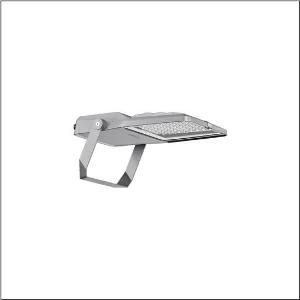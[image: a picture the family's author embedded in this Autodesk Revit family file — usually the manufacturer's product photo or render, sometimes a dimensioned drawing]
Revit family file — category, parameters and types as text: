
# Revit family: floodlight_fl_21_iq_mini___pl61_5xa7772c3c1a_b73e
name_source: partatom
category: Lighting Fixtures
units: mm (PartAtom-declared; Revit-internal decimal feet)

## family parameters
Cut with Voids When Loaded = No
Host = Face
Light Source = No
Part Type = Normal
Room Calculation Point = No
Round Connector Dimension = Use Diameter
Shared = No

## types (1)
- --- (1 x LED, 10320 lm, 87.2 W, 3000K)
    Apparent Load = 87 VA
    CIE Flux Codes = 33 65 98 100 100
    Color Rendering = 80
    Color Temperature = 3000K
    Default Elevation = 1800 mm
    Description = Floodlight FL 21 iQ mini, floodlight, primary light control with lens, of PMMA, primary optical cover: protective disc, of toughened safety glass, transparent, light distribution: PL61, light emission: direct distribution, installation type: surface-mounted, LED, High Power LED, rated luminous flux: 10.320lm, luminous efficacy: 118lm/W, light colour: 830, colour temperature: 3000K, control: Street-Remote, Auto-Match, Temp-Guard, Night-Set, Smart-Wire, Desk-Remote (wireless, voltage-free reading and setting of iQ features in the workshop via application-optimized NFC function/RFID function), optimised constant luminous flux control (CLO 2.0), with terminal, 6-pole, mains connection: 220..240V, AC, 50/60Hz, start of lifetime: 87W, end of service life: 92W, reduction: 40W, luminaire housing, of diecast aluminium, powder-coated, Siteco® metallic grey (DB 702S), corrosivity category C5 mid according to DIN EN ISO 12944, sealing non-destructively replaceable, mounting bracket, of steel, galvanised, powder-coated, Siteco® metallic grey (DB 702S), protection rating (complete): IP66, insulation class (complete): insulation class II (safety insulation), certification: CE, ENEC, VDE, protection symbol: D, impact resistance: IK08, permissible operating ambient temperature: -40..+40°C, permissible operating ambient temperature for outdoor applications: -40..+50°C, standard: DIN EN 12944, LABS conformity tested according to VDMA 24364:2018-05, packaging unit: 1 piece

Light Distribution: PL61
    Height = 70 mm
    Lamp = 1 x LED
    Lamp Light Flux = 10320 lm
    Lamp Power = 87.2 W
    Lamp count = 1
    Length = 485 mm
    Luminous efficacy = 118 lm/W
    Manufacturer = Siteco
    ModVariant = No
    Model = 5XA7772C3C1A
    Number of Poles = 1
    OnlyDefault = Yes
    Power Factor = 1
    Product Name = Floodlight FL 21 iQ mini | PL61
    Product group = floodlight | pylon annexe
    ProductGroupID = 6200
    Protection Class = Protection class II
    Protection Degree = IP 66
    RLX_Detail_Level = 1
    RLX_Emergency_Light_Flux = 0 lm
    RLX_Emergency_Type = 0
    RLX_Emergency_Type_DB = No
    RlxData = <blob elided: 96245 chars, md5=e113ce68>
    Socket = socket
    Standby Power = 0 W
    System Light Flux = 10320 lm
    System Power = 87 W
    Type Comments = factory setting: luminous flux: 100 % | dim-lin: 254 | 456 mA
    Type Image = l_1006845.jpg
    URL = http://relux.com
    VarID = @adj_106083
    Voltage = 0 V
    Weight = 0.00 kg
    Width = 337 mm

## geometry (parser evidence)
native form markers: Blend x4, Sweep x12
no freeform markers — native parametric forms only
